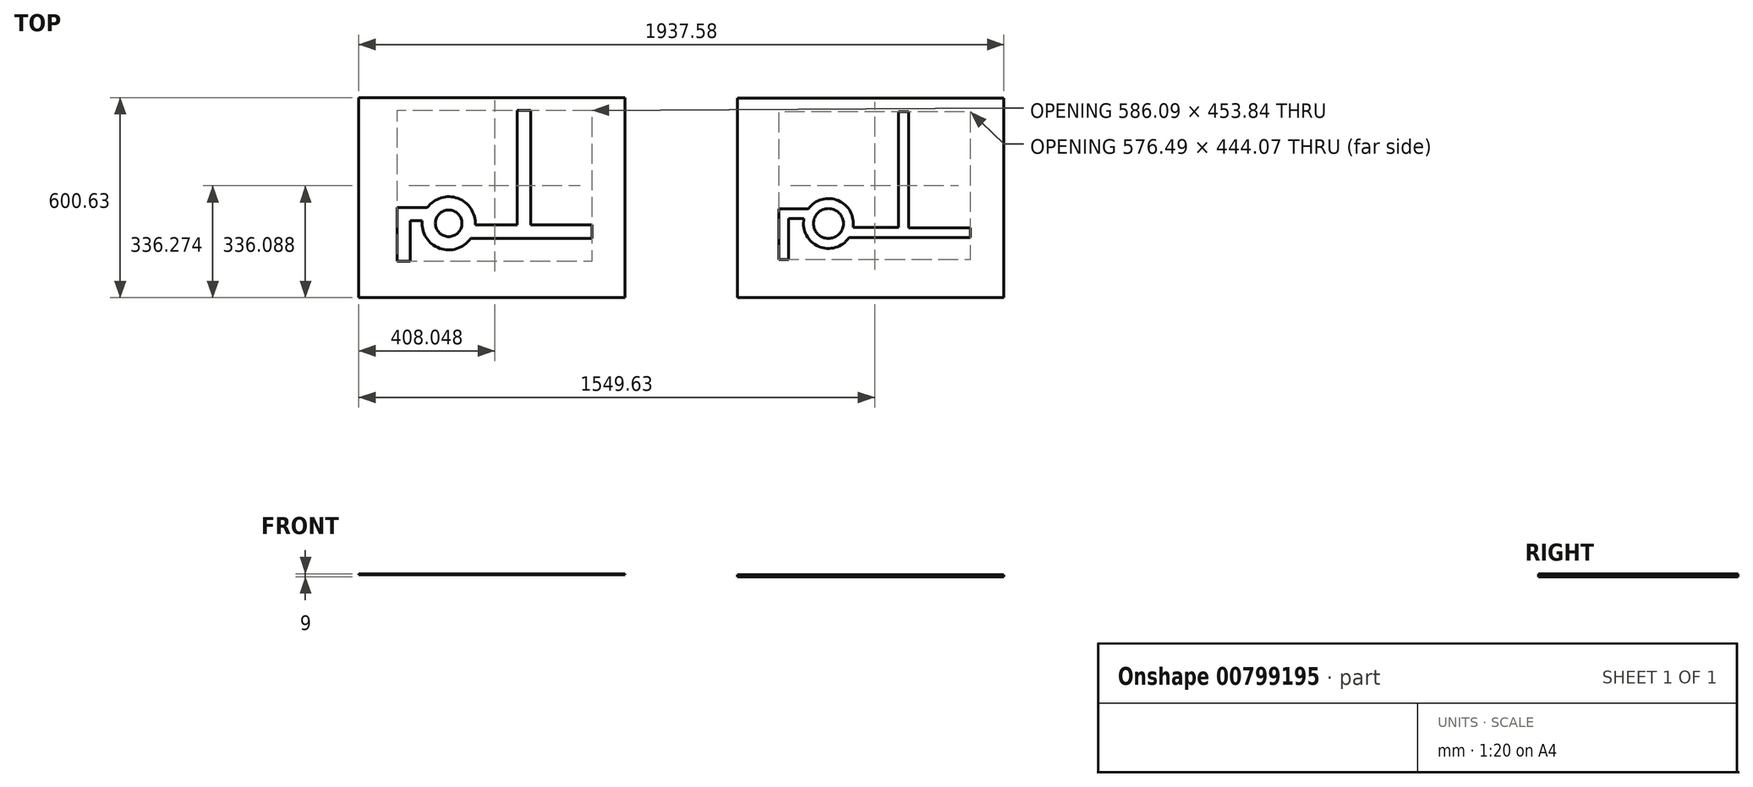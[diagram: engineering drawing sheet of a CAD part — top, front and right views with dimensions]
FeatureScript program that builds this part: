
annotation { "Feature Type Name" : "Feature", "Feature Type Description" : "" }
export const myFeature = defineFeature(function(context is Context, id is Id, definition is map)
    precondition{}
    {
        {
            var Q0;
            Q0=qCreatedBy(makeId("Top.planeOp"),FACE);
            var sketch = newSketch(context, id + "F0", { "sketchPlane" : qUnion([Q0])});
            skLineSegment(sketch, "E0.bottom", {"start": v(252.18, 324.04) * mm, "end": v(-547.82, 324.04) * mm});
            skLineSegment(sketch, "E0.top", {"start": v(252.18, -275.96) * mm, "end": v(-547.82, -275.96) * mm});
            skLineSegment(sketch, "E0.left", {"start": v(252.18, 324.04) * mm, "end": v(252.18, -275.96) * mm});
            skLineSegment(sketch, "E0.right", {"start": v(-547.82, 324.04) * mm, "end": v(-547.82, -275.96) * mm});
            skPoint(sketch, "E0.middle", {"position": v(-147.82, 24.04) * mm});
            skSolve(sketch);
        }
        {
            var Q0;
            Q0 = qSketchRegion(id + "F0", true);
            extrude(context, id + "F1", {"entities" : qUnion([Q0]), "depth" : 3 * mm, "offsetDistance" : 25 * mm});
        }
        {
            var Q0;
            Q0=qCreatedBy(makeId("Top.planeOp"),FACE);
            var sketch = newSketch(context, id + "F2", { "sketchPlane" : qUnion([Q0])});
            skLineSegment(sketch, "E1", {"start": v(-432.81, -167.42) * mm, "end": v(-392.81, -167.42) * mm});
            skLineSegment(sketch, "E2", {"start": v(-392.81, -167.42) * mm, "end": v(-392.81, -45.76) * mm});
            skLineSegment(sketch, "E3", {"start": v(-392.81, -45.76) * mm, "end": v(-357.43, -45.76) * mm});
            skArc(sketch, "E4", {"start": v(-357.43, -45.76) * mm, "mid": v(-305.02, -128.6) * mm, "end": v(-211.73, -98.49) * mm});
            skLineSegment(sketch, "E5", {"start": v(-432.81, -167.42) * mm, "end": v(-432.81, -5.76) * mm});
            skLineSegment(sketch, "E6", {"start": v(-432.81, -5.76) * mm, "end": v(-342.08, -5.76) * mm});
            skLineSegment(sketch, "E7", {"start": v(-197.96, -58.49) * mm, "end": v(-71.73, -58.49) * mm});
            skLineSegment(sketch, "E8", {"start": v(-71.73, -58.49) * mm, "end": v(-71.73, 286.42) * mm});
            skLineSegment(sketch, "E9", {"start": v(-71.73, 286.42) * mm, "end": v(-31.73, 286.42) * mm});
            skLineSegment(sketch, "E10", {"start": v(-31.73, 286.42) * mm, "end": v(-31.73, -58.58) * mm});
            skLineSegment(sketch, "E11", {"start": v(-31.73, -58.58) * mm, "end": v(153.27, -58.58) * mm});
            skLineSegment(sketch, "E12", {"start": v(153.27, -58.58) * mm, "end": v(153.27, -98.49) * mm});
            skLineSegment(sketch, "E13", {"start": v(153.27, -98.49) * mm, "end": v(-211.73, -98.49) * mm});
            skArc(sketch, "E14.trimOffspring", {"start": v(-197.96, -58.49) * mm, "mid": v(-250.3, 21.76) * mm, "end": v(-342.08, -5.76) * mm});
            skCircle(sketch, "E15", {"center": v(-277.8, -53.37) * mm, "radius": 40 * mm});
            skSolve(sketch);
        }
        {
            var Q0;
            Q0 = qSketchRegion(id + "F2", true);
            extrude(context, id + "F3", {"entities" : qUnion([Q0]), "operationType" : NewBodyOperationType.REMOVE, "depth" : 25 * mm, "offsetDistance" : 25 * mm, "hasSecondDirection" : true, "secondDirectionOppositeDirection" : true, "secondDirectionDepth" : 25 * mm});
        }
        {
            var Q0;
            Q0=qCreatedBy(makeId("Top.planeOp"),FACE);
            var sketch = newSketch(context, id + "F4", { "sketchPlane" : qUnion([Q0])});
            skLineSegment(sketch, "E16.bottom", {"start": v(1172.76, 333.41) * mm, "end": v(372.76, 333.41) * mm});
            skLineSegment(sketch, "E16.top", {"start": v(1172.76, -266.59) * mm, "end": v(372.76, -266.59) * mm});
            skLineSegment(sketch, "E16.left", {"start": v(1172.76, 333.41) * mm, "end": v(1172.76, -266.59) * mm});
            skLineSegment(sketch, "E16.right", {"start": v(372.76, 333.41) * mm, "end": v(372.76, -266.59) * mm});
            skPoint(sketch, "E16.middle", {"position": v(772.76, 33.41) * mm});
            skSolve(sketch);
        }
        {
            var Q0;
            Q0 = qSketchRegion(id + "F4", true);
            extrude(context, id + "F5", {"entities" : qUnion([Q0]), "depth" : 6 * mm, "offsetDistance" : 25 * mm});
        }
        {
            var Q0;
            Q0=qCreatedBy(makeId("Top.planeOp"),FACE);
            var sketch = newSketch(context, id + "F6", { "sketchPlane" : qUnion([Q0])});
            skLineSegment(sketch, "E17", {"start": v(-235.43, -145.35) * mm, "end": v(-205.43, -145.35) * mm});
            skLineSegment(sketch, "E18", {"start": v(-205.43, -145.35) * mm, "end": v(-205.43, -22.35) * mm});
            skLineSegment(sketch, "E19", {"start": v(-205.43, -22.35) * mm, "end": v(-159.43, -22.35) * mm});
            skArc(sketch, "E20", {"start": v(-159.43, -22.35) * mm, "mid": v(-114.93, -106.13) * mm, "end": v(-23.94, -79.28) * mm});
            skLineSegment(sketch, "E21", {"start": v(-235.43, -145.35) * mm, "end": v(-235.43, 7.65) * mm});
            skLineSegment(sketch, "E22", {"start": v(-235.43, 7.65) * mm, "end": v(-146.14, 7.65) * mm});
            skLineSegment(sketch, "E23", {"start": v(-11.89, -49.28) * mm, "end": v(125.11, -49.28) * mm});
            skLineSegment(sketch, "E24", {"start": v(125.11, -49.28) * mm, "end": v(125.11, 298.72) * mm});
            skLineSegment(sketch, "E25", {"start": v(125.11, 298.72) * mm, "end": v(155.11, 298.72) * mm});
            skLineSegment(sketch, "E26", {"start": v(155.11, 298.72) * mm, "end": v(155.11, -49.38) * mm});
            skLineSegment(sketch, "E27", {"start": v(155.11, -49.38) * mm, "end": v(341.06, -49.38) * mm});
            skLineSegment(sketch, "E28", {"start": v(341.06, -49.38) * mm, "end": v(341.06, -79.28) * mm});
            skLineSegment(sketch, "E29", {"start": v(341.06, -79.28) * mm, "end": v(-23.94, -79.28) * mm});
            skArc(sketch, "E30.trimOffspring", {"start": v(-11.89, -49.28) * mm, "mid": v(-56.6, 32.06) * mm, "end": v(-146.14, 7.65) * mm});
            skCircle(sketch, "E31", {"center": v(-85.87, -36.99) * mm, "radius": 45 * mm});
            skSolve(sketch);
        }
        {
            var Q0;
            Q0 = qSketchRegion(id + "F6", true);
            extrude(context, id + "F7", {"entities" : qUnion([Q0]), "depth" : 40 * mm, "offsetDistance" : 25 * mm, "hasSecondDirection" : true, "secondDirectionOppositeDirection" : true, "secondDirectionDepth" : -20 * mm});
        }
        {
            var Q0;
            Q0=makeQuery(id+"F7.opExtrude","SWEPT_BODY",BODY,{"disambiguationData":[OSD([sQuery(id+"F6.wireOp",EDGE,"E17"),sQuery(id+"F6.wireOp",EDGE,"E18"),sQuery(id+"F6.wireOp",EDGE,"E19"),sQuery(id+"F6.wireOp",EDGE,"E20"),sQuery(id+"F6.wireOp",EDGE,"E21"),sQuery(id+"F6.wireOp",EDGE,"E22"),sQuery(id+"F6.wireOp",EDGE,"E23"),sQuery(id+"F6.wireOp",EDGE,"E24"),sQuery(id+"F6.wireOp",EDGE,"E25"),sQuery(id+"F6.wireOp",EDGE,"E26"),sQuery(id+"F6.wireOp",EDGE,"E27"),sQuery(id+"F6.wireOp",EDGE,"E28"),sQuery(id+"F6.wireOp",EDGE,"E29"),sQuery(id+"F6.wireOp",EDGE,"E30.trimOffspring"),sQuery(id+"F6.wireOp",EDGE,"E31")])]});
            transform(context, id + "F8", {"entities" : qUnion([Q0]), "transformType" : TransformType.TRANSLATION_3D, "dx" : 740 * mm, "dy" : 0 * mm, "dz" : 0 * mm, "makeCopy" : false});
        }
        {
            var Q0;
            Q0=makeQuery(id+"F5.opExtrude","SWEPT_BODY",BODY,{"disambiguationData":[OSD([sQuery(id+"F4.wireOp",EDGE,"E16.bottom"),sQuery(id+"F4.wireOp",EDGE,"E16.top"),sQuery(id+"F4.wireOp",EDGE,"E16.left"),sQuery(id+"F4.wireOp",EDGE,"E16.right")])]});
            var Q1;
            Q1=makeQuery(id+"F7.opExtrude","SWEPT_BODY",BODY,{"disambiguationData":[OSD([sQuery(id+"F6.wireOp",EDGE,"E17"),sQuery(id+"F6.wireOp",EDGE,"E18"),sQuery(id+"F6.wireOp",EDGE,"E19"),sQuery(id+"F6.wireOp",EDGE,"E20"),sQuery(id+"F6.wireOp",EDGE,"E21"),sQuery(id+"F6.wireOp",EDGE,"E22"),sQuery(id+"F6.wireOp",EDGE,"E23"),sQuery(id+"F6.wireOp",EDGE,"E24"),sQuery(id+"F6.wireOp",EDGE,"E25"),sQuery(id+"F6.wireOp",EDGE,"E26"),sQuery(id+"F6.wireOp",EDGE,"E27"),sQuery(id+"F6.wireOp",EDGE,"E28"),sQuery(id+"F6.wireOp",EDGE,"E29"),sQuery(id+"F6.wireOp",EDGE,"E30.trimOffspring"),sQuery(id+"F6.wireOp",EDGE,"E31")])]});
            transform(context, id + "F9", {"entities" : qUnion([Q0, Q1]), "transformType" : TransformType.TRANSLATION_3D, "dx" : -924 * mm, "dy" : -10 * mm, "dz" : -6 * mm, "makeCopy" : false});
        }
        {
            var Q0;
            Q0=makeQuery(id+"F7.opExtrude","SWEPT_BODY",BODY,{"disambiguationData":[OSD([sQuery(id+"F6.wireOp",EDGE,"E17"),sQuery(id+"F6.wireOp",EDGE,"E18"),sQuery(id+"F6.wireOp",EDGE,"E19"),sQuery(id+"F6.wireOp",EDGE,"E20"),sQuery(id+"F6.wireOp",EDGE,"E21"),sQuery(id+"F6.wireOp",EDGE,"E22"),sQuery(id+"F6.wireOp",EDGE,"E23"),sQuery(id+"F6.wireOp",EDGE,"E24"),sQuery(id+"F6.wireOp",EDGE,"E25"),sQuery(id+"F6.wireOp",EDGE,"E26"),sQuery(id+"F6.wireOp",EDGE,"E27"),sQuery(id+"F6.wireOp",EDGE,"E28"),sQuery(id+"F6.wireOp",EDGE,"E29"),sQuery(id+"F6.wireOp",EDGE,"E30.trimOffspring"),sQuery(id+"F6.wireOp",EDGE,"E31")])]});
            transform(context, id + "F10", {"entities" : qUnion([Q0]), "transformType" : TransformType.TRANSLATION_3D, "dx" : -8 * mm, "dy" : -7 * mm, "dz" : -25 * mm, "makeCopy" : false});
        }
        {
            var Q0;
            Q0=makeQuery(id+"F7.opExtrude","SWEPT_BODY",BODY,{"disambiguationData":[OSD([sQuery(id+"F6.wireOp",EDGE,"E17"),sQuery(id+"F6.wireOp",EDGE,"E18"),sQuery(id+"F6.wireOp",EDGE,"E19"),sQuery(id+"F6.wireOp",EDGE,"E20"),sQuery(id+"F6.wireOp",EDGE,"E21"),sQuery(id+"F6.wireOp",EDGE,"E22"),sQuery(id+"F6.wireOp",EDGE,"E23"),sQuery(id+"F6.wireOp",EDGE,"E24"),sQuery(id+"F6.wireOp",EDGE,"E25"),sQuery(id+"F6.wireOp",EDGE,"E26"),sQuery(id+"F6.wireOp",EDGE,"E27"),sQuery(id+"F6.wireOp",EDGE,"E28"),sQuery(id+"F6.wireOp",EDGE,"E29"),sQuery(id+"F6.wireOp",EDGE,"E30.trimOffspring"),sQuery(id+"F6.wireOp",EDGE,"E31")])]});
            var Q1;
            Q1=makeQuery(id+"F5.opExtrude","SWEPT_BODY",BODY,{"disambiguationData":[OSD([sQuery(id+"F4.wireOp",EDGE,"E16.bottom"),sQuery(id+"F4.wireOp",EDGE,"E16.top"),sQuery(id+"F4.wireOp",EDGE,"E16.left"),sQuery(id+"F4.wireOp",EDGE,"E16.right")])]});
            transform(context, id + "F11", {"entities" : qUnion([Q0, Q1]), "transformType" : TransformType.TRANSLATION_3D, "dx" : 1025 * mm, "dy" : 0 * mm, "dz" : 0 * mm, "makeCopy" : false});
        }
        {
            var Q0;
            Q0=makeQuery(id+"F7.opExtrude","SWEPT_BODY",BODY,{"disambiguationData":[OSD([sQuery(id+"F6.wireOp",EDGE,"E17"),sQuery(id+"F6.wireOp",EDGE,"E18"),sQuery(id+"F6.wireOp",EDGE,"E19"),sQuery(id+"F6.wireOp",EDGE,"E20"),sQuery(id+"F6.wireOp",EDGE,"E21"),sQuery(id+"F6.wireOp",EDGE,"E22"),sQuery(id+"F6.wireOp",EDGE,"E23"),sQuery(id+"F6.wireOp",EDGE,"E24"),sQuery(id+"F6.wireOp",EDGE,"E25"),sQuery(id+"F6.wireOp",EDGE,"E26"),sQuery(id+"F6.wireOp",EDGE,"E27"),sQuery(id+"F6.wireOp",EDGE,"E28"),sQuery(id+"F6.wireOp",EDGE,"E29"),sQuery(id+"F6.wireOp",EDGE,"E30.trimOffspring"),sQuery(id+"F6.wireOp",EDGE,"E31")])]});
            var Q1;
            Q1=makeQuery(id+"F5.opExtrude","SWEPT_BODY",BODY,{"disambiguationData":[OSD([sQuery(id+"F4.wireOp",EDGE,"E16.bottom"),sQuery(id+"F4.wireOp",EDGE,"E16.top"),sQuery(id+"F4.wireOp",EDGE,"E16.left"),sQuery(id+"F4.wireOp",EDGE,"E16.right")])]});
            booleanBodies(context, id + "F12", {"operationType" : BooleanOperationType.SUBTRACTION, "tools" : qUnion([Q0]), "targets" : qUnion([Q1])});
        }
        {
            var Q0;
            Q0=makeQuery(id+"F12.opBoolean","SPLIT",BODY,{"disambiguationData":[OD(0.0)],"derivedFrom":makeQuery(id+"F5.opExtrude","SWEPT_BODY",BODY,{"disambiguationData":[OSD([sQuery(id+"F4.wireOp",EDGE,"E16.bottom"),sQuery(id+"F4.wireOp",EDGE,"E16.top"),sQuery(id+"F4.wireOp",EDGE,"E16.left"),sQuery(id+"F4.wireOp",EDGE,"E16.right")])]})});
            var Q1;
            Q1=makeQuery(id+"F12.opBoolean","SPLIT",BODY,{"disambiguationData":[OD(1.0)],"derivedFrom":makeQuery(id+"F5.opExtrude","SWEPT_BODY",BODY,{"disambiguationData":[OSD([sQuery(id+"F4.wireOp",EDGE,"E16.bottom"),sQuery(id+"F4.wireOp",EDGE,"E16.top"),sQuery(id+"F4.wireOp",EDGE,"E16.left"),sQuery(id+"F4.wireOp",EDGE,"E16.right")])]})});
            transform(context, id + "F13", {"entities" : qUnion([Q0, Q1]), "transformType" : TransformType.TRANSLATION_3D, "dx" : 116 * mm, "dy" : 0 * mm, "dz" : 0 * mm, "makeCopy" : false});
        }
    });
